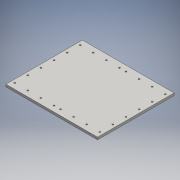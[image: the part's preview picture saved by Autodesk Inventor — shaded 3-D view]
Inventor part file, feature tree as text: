
AUTODESK INVENTOR PART (.ipt)
format: ipt  version: 2016 (Build 200138000, 138)  size: 145,920 bytes
history: native  units: mm
features: reference x20, extrude x1, sketch x1
ambient origin geometry x8: Origin, YZ Plane, XZ Plane, XY Plane, X Axis, Y Axis, Z Axis, Center Point
bodies: Body1 (feature_tree)
feature tree (22):
  extrude  "Extrusion9"  Depth=187.0mm
  sketch  "Sketch1"  dims[d0=224.0mm d1=187.0mm d36=32.0mm d37=32.0mm d38=32.0mm d39=16.0mm d40=32.0mm d41=32.0mm d42=32.0mm d43=32.0mm d44=32.0mm d45=32.0mm d46=32.0mm d47=32.0mm d48=8.0mm d49=13.5mm d50=32.0mm d51=32.0mm d52=32.0mm d53=16.0mm d54=32.0mm d55=32.0mm d56=32.0mm d57=32.0mm d58=32.0mm d59=32.0mm d60=32.0mm d61=32.0mm d62=13.5mm d63=8.0mm d64=8.0mm d65=13.5mm d66=8.0mm d67=13.5mm d68=6.0mm d69=0.0mm]
  reference  "Reference2"
  reference  "Reference4"
  reference  "Reference6"
  reference  "Reference7"
  reference  "Reference9"
  reference  "Reference11"
  reference  "Reference14"
  reference  "Reference16"
  reference  "Reference18"
  reference  "Reference19"
  reference  "Reference21"
  reference  "Reference23"
  reference  "Reference70"
  reference  "Reference72"
  reference  "Reference74"
  reference  "Reference76"
  reference  "Reference80"
  reference  "Reference84"
  reference  "Reference88"
  reference  "Reference93"
